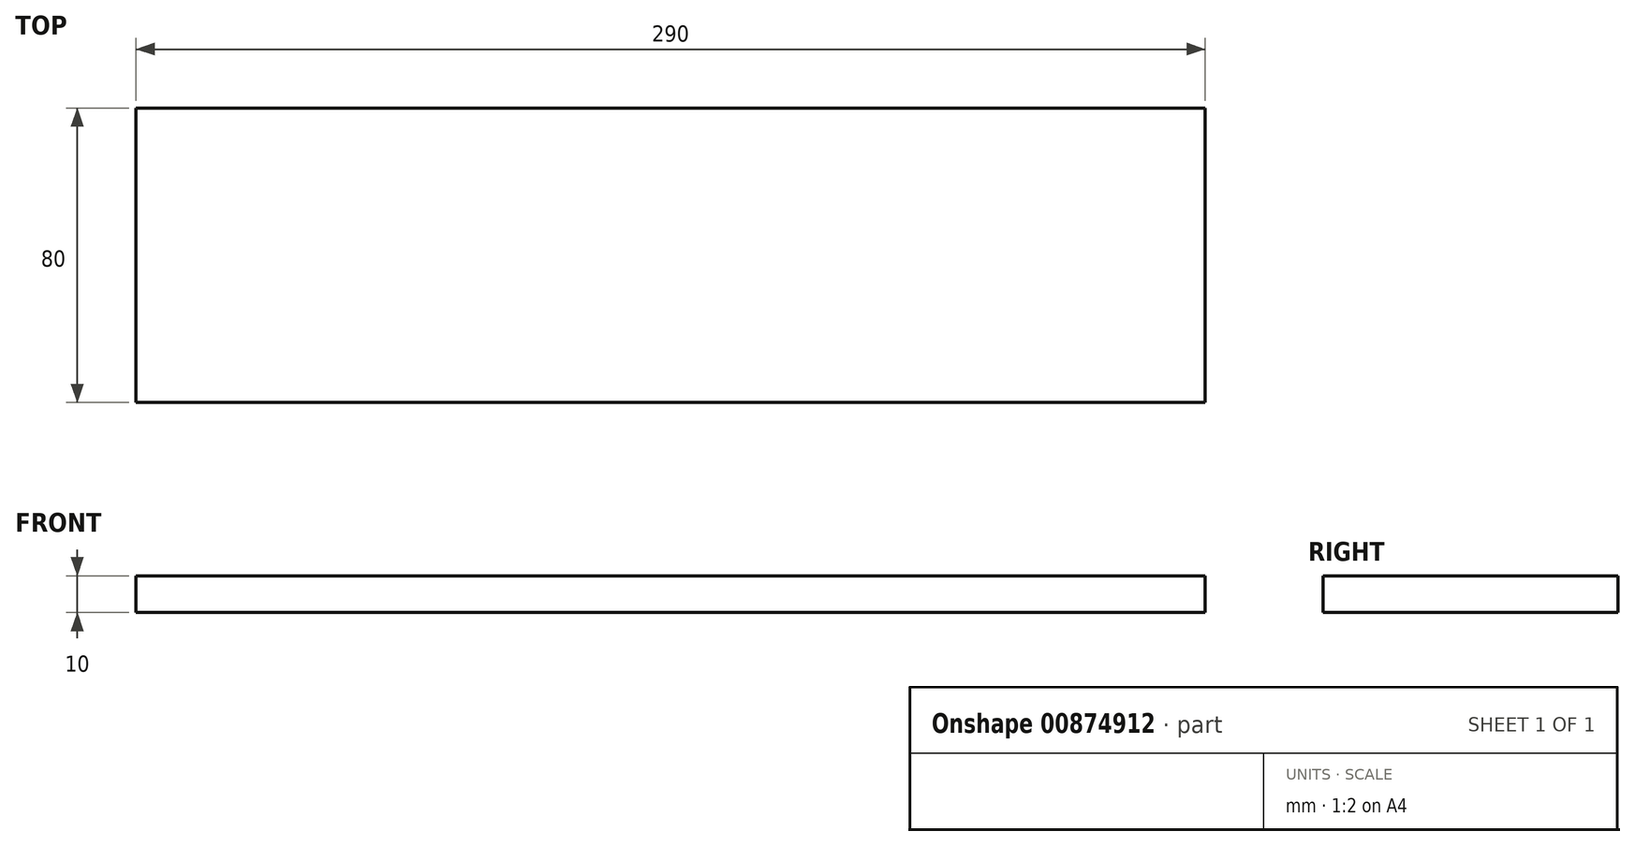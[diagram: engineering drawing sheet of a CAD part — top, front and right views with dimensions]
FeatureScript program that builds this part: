
annotation { "Feature Type Name" : "Feature", "Feature Type Description" : "" }
export const myFeature = defineFeature(function(context is Context, id is Id, definition is map)
    precondition{}
    {
        {
            var Q0;
            Q0=qCreatedBy(makeId("Top.planeOp"),FACE);
            var sketch = newSketch(context, id + "F0", { "sketchPlane" : qUnion([Q0])});
            skLineSegment(sketch, "E0.bottom", {"start": v(145, 40) * mm, "end": v(-145, 40) * mm});
            skLineSegment(sketch, "E0.top", {"start": v(145, -40) * mm, "end": v(-145, -40) * mm});
            skLineSegment(sketch, "E0.left", {"start": v(145, 40) * mm, "end": v(145, -40) * mm});
            skLineSegment(sketch, "E0.right", {"start": v(-145, 40) * mm, "end": v(-145, -40) * mm});
            skPoint(sketch, "E0.middle", {"position": v(0, 0) * mm});
            skSolve(sketch);
        }
        {
            var Q0;
            Q0 = qSketchRegion(id + "F0", true);
            extrude(context, id + "F1", {"entities" : qUnion([Q0]), "depth" : 10 * mm, "offsetDistance" : 25 * mm});
        }
    });
